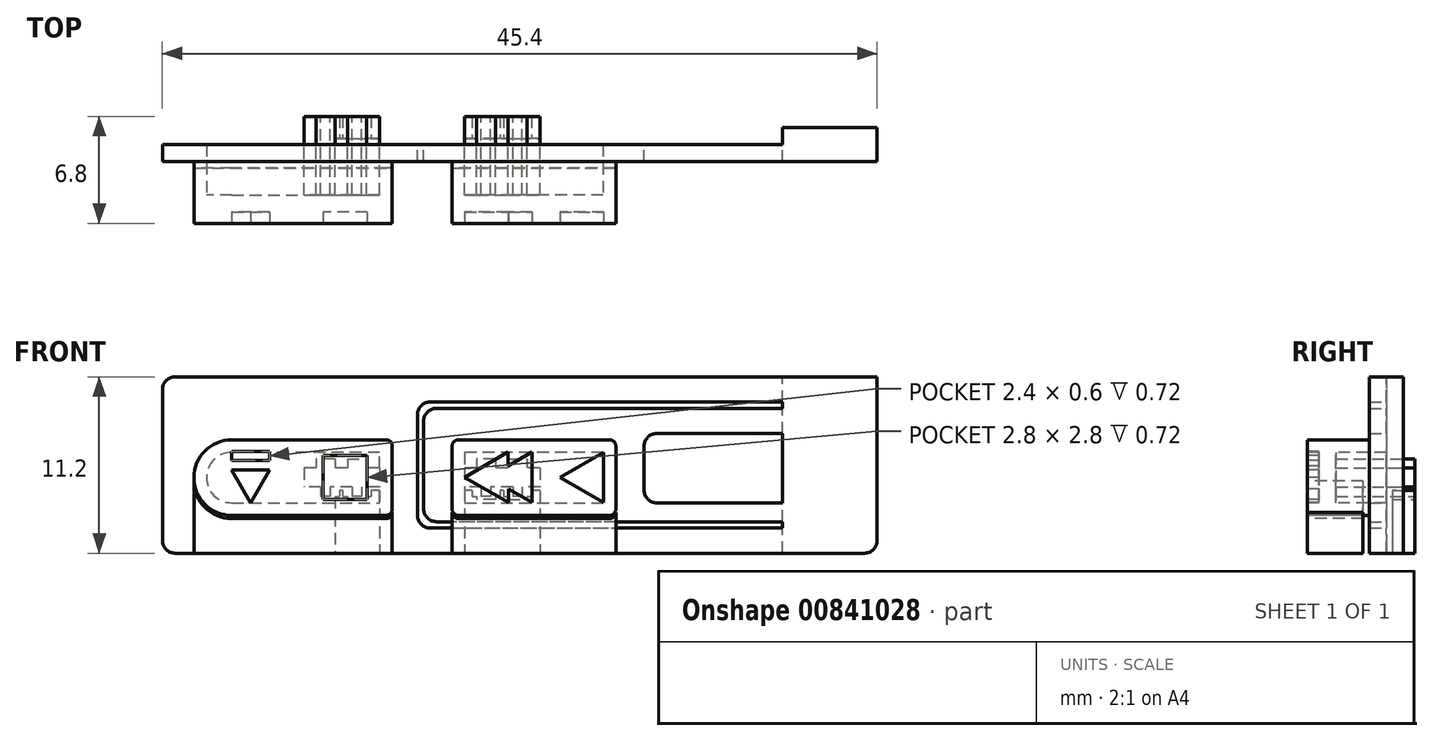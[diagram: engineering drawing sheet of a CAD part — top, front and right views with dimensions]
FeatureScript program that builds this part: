
annotation { "Feature Type Name" : "Feature", "Feature Type Description" : "" }
export const myFeature = defineFeature(function(context is Context, id is Id, definition is map)
    precondition{}
    {
        {
            var Q0;
            Q0=qCreatedBy(makeId("Front.planeOp"),FACE);
            var sketch = newSketch(context, id + "F0", { "sketchPlane" : qUnion([Q0])});
            skLineSegment(sketch, "E0.bottom", {"start": v(12.92, 2.7) * mm, "end": v(1.92, 2.7) * mm, "construction": true});
            skLineSegment(sketch, "E0.top", {"start": v(12.92, -2.7) * mm, "end": v(1.92, -2.7) * mm, "construction": true});
            skLineSegment(sketch, "E0.left", {"start": v(12.92, 2.7) * mm, "end": v(12.92, -2.7) * mm, "construction": true});
            skLineSegment(sketch, "E0.right", {"start": v(1.92, 2.7) * mm, "end": v(1.92, -2.7) * mm, "construction": true});
            skLineSegment(sketch, "E1.bottom", {"start": v(-1.28, 2.7) * mm, "end": v(-11.78, 2.7) * mm, "construction": true});
            skLineSegment(sketch, "E1.top", {"start": v(-1.28, -2.7) * mm, "end": v(-11.78, -2.7) * mm, "construction": true});
            skLineSegment(sketch, "E1.left", {"start": v(-1.28, 2.7) * mm, "end": v(-1.28, -2.7) * mm, "construction": true});
            skArc(sketch, "E2", {"start": v(-11.78, 2.7) * mm, "mid": v(-14.48, 0) * mm, "end": v(-11.78, -2.7) * mm, "construction": true});
            skLineSegment(sketch, "E3.0", {"start": v(-1.58, 2.4) * mm, "end": v(-11.78, 2.4) * mm});
            skLineSegment(sketch, "E3.1", {"start": v(-1.58, 2.4) * mm, "end": v(-1.58, -2.4) * mm});
            skLineSegment(sketch, "E3.2", {"start": v(-1.58, -2.4) * mm, "end": v(-11.78, -2.4) * mm});
            skArc(sketch, "E3.3", {"start": v(-11.78, 2.4) * mm, "mid": v(-14.18, 0) * mm, "end": v(-11.78, -2.4) * mm});
            skLineSegment(sketch, "E4.0", {"start": v(12.62, 2.4) * mm, "end": v(2.22, 2.4) * mm});
            skLineSegment(sketch, "E4.1", {"start": v(12.62, 2.4) * mm, "end": v(12.62, -2.4) * mm});
            skLineSegment(sketch, "E4.2", {"start": v(12.62, -2.4) * mm, "end": v(2.22, -2.4) * mm});
            skLineSegment(sketch, "E4.3", {"start": v(2.22, 2.4) * mm, "end": v(2.22, -2.4) * mm});
            skLineSegment(sketch, "E5.0", {"start": v(-2.38, 1.6) * mm, "end": v(-11.78, 1.6) * mm});
            skLineSegment(sketch, "E5.1", {"start": v(-2.38, 1.6) * mm, "end": v(-2.38, -1.6) * mm});
            skLineSegment(sketch, "E5.2", {"start": v(-2.38, -1.6) * mm, "end": v(-11.78, -1.6) * mm});
            skArc(sketch, "E5.3", {"start": v(-11.78, 1.6) * mm, "mid": v(-13.38, 0) * mm, "end": v(-11.78, -1.6) * mm});
            skLineSegment(sketch, "E6.0", {"start": v(3.02, 1.6) * mm, "end": v(3.02, -1.6) * mm});
            skLineSegment(sketch, "E6.1", {"start": v(11.82, 1.6) * mm, "end": v(3.02, 1.6) * mm});
            skLineSegment(sketch, "E6.2", {"start": v(11.82, 1.6) * mm, "end": v(11.82, -1.6) * mm});
            skLineSegment(sketch, "E6.3", {"start": v(11.82, -1.6) * mm, "end": v(3.02, -1.6) * mm});
            skLineSegment(sketch, "E7.0", {"start": v(0.02, 6.4) * mm, "end": v(0.02, -4.8) * mm});
            skLineSegment(sketch, "E8.0", {"start": v(0.42, 4.4) * mm, "end": v(0.42, -2.8) * mm});
            skLineSegment(sketch, "E9.0", {"start": v(29.22, 6.4) * mm, "end": v(-16.18, 6.4) * mm});
            skLineSegment(sketch, "E10.0", {"start": v(23.22, -4.8) * mm, "end": v(-16.18, -4.8) * mm});
            skLineSegment(sketch, "E11", {"start": v(-16.18, 6.4) * mm, "end": v(-16.18, -4.8) * mm});
            skLineSegment(sketch, "E12.0", {"start": v(23.22, 4.4) * mm, "end": v(0.42, 4.4) * mm});
            skLineSegment(sketch, "E13.MirrorCS", {"start": v(23.22, -2.8) * mm, "end": v(0.42, -2.8) * mm});
            skLineSegment(sketch, "E14.0", {"start": v(23.22, 4.8) * mm, "end": v(0.02, 4.8) * mm});
            skLineSegment(sketch, "E15", {"start": v(0.02, -3.2) * mm, "end": v(23.22, -3.2) * mm});
            skLineSegment(sketch, "E16", {"start": v(14.42, 4.4) * mm, "end": v(14.42, -2.8) * mm});
            skLineSegment(sketch, "E17", {"start": v(14.42, 2.8) * mm, "end": v(23.22, 2.8) * mm});
            skLineSegment(sketch, "E18", {"start": v(14.42, -1.6) * mm, "end": v(23.22, -1.6) * mm});
            skLineSegment(sketch, "E19", {"start": v(29.22, 6.4) * mm, "end": v(29.22, -4.8) * mm});
            skLineSegment(sketch, "E20", {"start": v(29.22, -4.8) * mm, "end": v(23.22, -4.8) * mm});
            skLineSegment(sketch, "E21", {"start": v(23.22, -4.8) * mm, "end": v(23.22, 6.4) * mm});
            skLineSegment(sketch, "E22.bottom", {"start": v(-2.38, 0.6) * mm, "end": v(-3.22, 0.6) * mm});
            skLineSegment(sketch, "E22.top", {"start": v(-2.38, -0.6) * mm, "end": v(-3.22, -0.6) * mm});
            skLineSegment(sketch, "E22.left", {"start": v(-2.38, 0.6) * mm, "end": v(-2.38, -0.6) * mm});
            skLineSegment(sketch, "E22.right", {"start": v(-7.18, 0.6) * mm, "end": v(-7.18, -0.6) * mm});
            skPoint(sketch, "E22.middle", {"position": v(-4.82, 0) * mm});
            skLineSegment(sketch, "E23.bottom", {"start": v(-5.22, 1.2) * mm, "end": v(-6.42, 1.2) * mm});
            skLineSegment(sketch, "E23.top", {"start": v(-5.22, -1.2) * mm, "end": v(-6.42, -1.2) * mm});
            skLineSegment(sketch, "E23.left", {"start": v(-5.22, 1.2) * mm, "end": v(-5.22, 0.6) * mm});
            skLineSegment(sketch, "E23.right", {"start": v(-6.42, 1.2) * mm, "end": v(-6.42, 0.6) * mm});
            skPoint(sketch, "E23.middle", {"position": v(-5.82, 0) * mm});
            skLineSegment(sketch, "E24", {"start": v(-4.82, 0.6) * mm, "end": v(-4.82, -0.6) * mm, "construction": true});
            skLineSegment(sketch, "E25.MirrorCS", {"start": v(-4.42, 1.2) * mm, "end": v(-4.42, 0.6) * mm});
            skLineSegment(sketch, "E26.MirrorCS", {"start": v(-3.22, 1.2) * mm, "end": v(-3.22, 0.6) * mm});
            skLineSegment(sketch, "E27.MirrorCS", {"start": v(-4.42, 1.2) * mm, "end": v(-3.22, 1.2) * mm});
            skLineSegment(sketch, "E28.MirrorCS", {"start": v(-4.42, -1.2) * mm, "end": v(-3.22, -1.2) * mm});
            skLineSegment(sketch, "E29.bottom", {"start": v(7.82, 0.6) * mm, "end": v(6.98, 0.6) * mm});
            skLineSegment(sketch, "E29.top", {"start": v(7.82, -0.6) * mm, "end": v(6.98, -0.6) * mm});
            skLineSegment(sketch, "E29.left", {"start": v(7.82, 0.6) * mm, "end": v(7.82, -0.6) * mm});
            skLineSegment(sketch, "E29.right", {"start": v(3.02, 0.6) * mm, "end": v(3.02, -0.6) * mm});
            skPoint(sketch, "E29.middle", {"position": v(5.38, 0) * mm});
            skLineSegment(sketch, "E30.bottom", {"start": v(4.98, 1.2) * mm, "end": v(3.78, 1.2) * mm});
            skLineSegment(sketch, "E30.top", {"start": v(4.98, -1.2) * mm, "end": v(3.78, -1.2) * mm});
            skLineSegment(sketch, "E30.left", {"start": v(4.98, 1.2) * mm, "end": v(4.98, 0.6) * mm});
            skLineSegment(sketch, "E30.right", {"start": v(3.78, 1.2) * mm, "end": v(3.78, 0.6) * mm});
            skPoint(sketch, "E30.middle", {"position": v(4.38, 0) * mm});
            skLineSegment(sketch, "E31", {"start": v(5.38, 0.6) * mm, "end": v(5.38, -0.6) * mm, "construction": true});
            skLineSegment(sketch, "E32.MirrorCS", {"start": v(5.78, 1.2) * mm, "end": v(5.78, 0.6) * mm});
            skLineSegment(sketch, "E33.MirrorCS", {"start": v(6.98, 1.2) * mm, "end": v(6.98, 0.6) * mm});
            skLineSegment(sketch, "E34.MirrorCS", {"start": v(5.78, 1.2) * mm, "end": v(6.98, 1.2) * mm});
            skLineSegment(sketch, "E35.MirrorCS", {"start": v(5.78, -1.2) * mm, "end": v(6.98, -1.2) * mm});
            skLineSegment(sketch, "E36", {"start": v(-6.42, 0.6) * mm, "end": v(-7.18, 0.6) * mm});
            skLineSegment(sketch, "E37", {"start": v(-6.42, -0.6) * mm, "end": v(-6.42, -1.2) * mm});
            skLineSegment(sketch, "E38", {"start": v(-6.42, -0.6) * mm, "end": v(-7.18, -0.6) * mm});
            skLineSegment(sketch, "E39", {"start": v(-5.22, -0.6) * mm, "end": v(-5.22, -1.2) * mm});
            skLineSegment(sketch, "E40", {"start": v(-4.42, -0.6) * mm, "end": v(-4.42, -1.2) * mm});
            skLineSegment(sketch, "E41", {"start": v(-4.42, -0.6) * mm, "end": v(-5.22, -0.6) * mm});
            skLineSegment(sketch, "E42", {"start": v(-4.42, 0.6) * mm, "end": v(-5.22, 0.6) * mm});
            skLineSegment(sketch, "E43.trimOffspring", {"start": v(-3.22, -0.6) * mm, "end": v(-3.22, -1.2) * mm});
            skLineSegment(sketch, "E44.trimOffspring", {"start": v(3.78, 0.6) * mm, "end": v(3.02, 0.6) * mm});
            skLineSegment(sketch, "E45.trimOffspring", {"start": v(3.78, -0.6) * mm, "end": v(3.78, -1.2) * mm});
            skLineSegment(sketch, "E46.trimOffspring", {"start": v(3.78, -0.6) * mm, "end": v(3.02, -0.6) * mm});
            skLineSegment(sketch, "E47.trimOffspring", {"start": v(4.98, -0.6) * mm, "end": v(4.98, -1.2) * mm});
            skLineSegment(sketch, "E48.trimOffspring", {"start": v(5.78, 0.6) * mm, "end": v(4.98, 0.6) * mm});
            skLineSegment(sketch, "E49.trimOffspring", {"start": v(6.98, -0.6) * mm, "end": v(6.98, -1.2) * mm});
            skLineSegment(sketch, "E50.trimOffspring", {"start": v(5.78, -0.6) * mm, "end": v(4.98, -0.6) * mm});
            skLineSegment(sketch, "E51.trimOffspring", {"start": v(5.78, -0.6) * mm, "end": v(5.78, -1.2) * mm});
            skSolve(sketch);
        }
        {
            var Q0;
            Q0=makeQuery(id+"F0.imprint","IMPRINT",FACE,{"disambiguationData":[TD([[makeQuery(id+"F0.imprint","IMPRINT",EDGE,{"derivedFrom":sQuery(id+"F0.wireOp",EDGE,"E22.bottom")}),1.0]])]});
            var Q1;
            Q1=makeQuery(id+"F0.imprint","IMPRINT",FACE,{"disambiguationData":[TD([[makeQuery(id+"F0.imprint","IMPRINT",EDGE,{"derivedFrom":sQuery(id+"F0.wireOp",EDGE,"E29.bottom")}),1.0]])]});
            extrude(context, id + "F1", {"entities" : qUnion([Q0, Q1]), "depth" : 6.8 * mm, "offsetDistance" : 25 * mm});
        }
        {
            var Q0;
            Q0=makeQuery(id+"F1.opExtrude","CAP_FACE",FACE,{"disambiguationData":[OSD([sQuery(id+"F0.wireOp",EDGE,"E22.bottom"),sQuery(id+"F0.wireOp",EDGE,"E22.top"),sQuery(id+"F0.wireOp",EDGE,"E22.left"),sQuery(id+"F0.wireOp",EDGE,"E22.right"),sQuery(id+"F0.wireOp",EDGE,"E23.bottom"),sQuery(id+"F0.wireOp",EDGE,"E23.top"),sQuery(id+"F0.wireOp",EDGE,"E23.left"),sQuery(id+"F0.wireOp",EDGE,"E23.right"),sQuery(id+"F0.wireOp",EDGE,"E25.MirrorCS"),sQuery(id+"F0.wireOp",EDGE,"E26.MirrorCS"),sQuery(id+"F0.wireOp",EDGE,"E27.MirrorCS"),sQuery(id+"F0.wireOp",EDGE,"E28.MirrorCS"),sQuery(id+"F0.wireOp",EDGE,"E36"),sQuery(id+"F0.wireOp",EDGE,"E37"),sQuery(id+"F0.wireOp",EDGE,"E38"),sQuery(id+"F0.wireOp",EDGE,"E39"),sQuery(id+"F0.wireOp",EDGE,"E40"),sQuery(id+"F0.wireOp",EDGE,"E41"),sQuery(id+"F0.wireOp",EDGE,"E42"),sQuery(id+"F0.wireOp",EDGE,"E43.trimOffspring")])],"isStart":false});
            var Q1;
            Q1=makeQuery(id+"F1.opExtrude","CAP_FACE",FACE,{"disambiguationData":[OSD([sQuery(id+"F0.wireOp",EDGE,"E29.bottom"),sQuery(id+"F0.wireOp",EDGE,"E29.top"),sQuery(id+"F0.wireOp",EDGE,"E29.left"),sQuery(id+"F0.wireOp",EDGE,"E29.right"),sQuery(id+"F0.wireOp",EDGE,"E30.bottom"),sQuery(id+"F0.wireOp",EDGE,"E30.top"),sQuery(id+"F0.wireOp",EDGE,"E30.left"),sQuery(id+"F0.wireOp",EDGE,"E30.right"),sQuery(id+"F0.wireOp",EDGE,"E32.MirrorCS"),sQuery(id+"F0.wireOp",EDGE,"E33.MirrorCS"),sQuery(id+"F0.wireOp",EDGE,"E34.MirrorCS"),sQuery(id+"F0.wireOp",EDGE,"E35.MirrorCS"),sQuery(id+"F0.wireOp",EDGE,"E44.trimOffspring"),sQuery(id+"F0.wireOp",EDGE,"E45.trimOffspring"),sQuery(id+"F0.wireOp",EDGE,"E46.trimOffspring"),sQuery(id+"F0.wireOp",EDGE,"E47.trimOffspring"),sQuery(id+"F0.wireOp",EDGE,"E48.trimOffspring"),sQuery(id+"F0.wireOp",EDGE,"E49.trimOffspring"),sQuery(id+"F0.wireOp",EDGE,"E50.trimOffspring"),sQuery(id+"F0.wireOp",EDGE,"E51.trimOffspring")])],"isStart":false});
            cPlane(context, id + "F2", {"entities" : qUnion([Q0, Q1]), "cplaneType" : CPlaneType.MID_PLANE, "offset" : 25 * mm, "width" : 150 * mm, "height" : 150 * mm});
        }
        {
            var Q0;
            Q0=qCreatedBy(id+"F2.planeOp",FACE);
            var sketch = newSketch(context, id + "F3", { "sketchPlane" : qUnion([Q0])});
            skLineSegment(sketch, "E52.0.0", {"start": v(-1.58, 2.4) * mm, "end": v(-11.78, 2.4) * mm});
            skArc(sketch, "E52.0.1", {"start": v(-11.78, 2.4) * mm, "mid": v(-14.18, 0) * mm, "end": v(-11.78, -2.4) * mm});
            skLineSegment(sketch, "E52.0.2", {"start": v(-11.78, -2.4) * mm, "end": v(-1.58, -2.4) * mm});
            skLineSegment(sketch, "E52.0.3", {"start": v(-1.58, -2.4) * mm, "end": v(-1.58, 2.4) * mm});
            skLineSegment(sketch, "E52.1.0", {"start": v(-6.42, -1.2) * mm, "end": v(-6.42, -0.6) * mm});
            skLineSegment(sketch, "E52.1.1", {"start": v(-6.42, -0.6) * mm, "end": v(-7.18, -0.6) * mm});
            skLineSegment(sketch, "E52.1.2", {"start": v(-7.18, -0.6) * mm, "end": v(-7.18, 0.6) * mm});
            skLineSegment(sketch, "E52.1.3", {"start": v(-7.18, 0.6) * mm, "end": v(-6.42, 0.6) * mm});
            skLineSegment(sketch, "E52.1.4", {"start": v(-6.42, 0.6) * mm, "end": v(-6.42, 1.2) * mm});
            skLineSegment(sketch, "E52.1.5", {"start": v(-6.42, 1.2) * mm, "end": v(-5.22, 1.2) * mm});
            skLineSegment(sketch, "E52.1.6", {"start": v(-5.22, 1.2) * mm, "end": v(-5.22, 0.6) * mm});
            skLineSegment(sketch, "E52.1.7", {"start": v(-5.22, 0.6) * mm, "end": v(-4.42, 0.6) * mm});
            skLineSegment(sketch, "E52.1.8", {"start": v(-4.42, 0.6) * mm, "end": v(-4.42, 1.2) * mm});
            skLineSegment(sketch, "E52.1.9", {"start": v(-4.42, 1.2) * mm, "end": v(-3.22, 1.2) * mm});
            skLineSegment(sketch, "E52.1.10", {"start": v(-3.22, 1.2) * mm, "end": v(-3.22, 0.6) * mm});
            skLineSegment(sketch, "E52.1.11", {"start": v(-3.22, 0.6) * mm, "end": v(-2.38, 0.6) * mm});
            skLineSegment(sketch, "E52.1.12", {"start": v(-2.38, 0.6) * mm, "end": v(-2.38, 1.6) * mm});
            skLineSegment(sketch, "E52.1.13", {"start": v(-2.38, 1.6) * mm, "end": v(-11.78, 1.6) * mm});
            skArc(sketch, "E52.1.14", {"start": v(-11.78, 1.6) * mm, "mid": v(-13.38, 0) * mm, "end": v(-11.78, -1.6) * mm});
            skLineSegment(sketch, "E52.1.15", {"start": v(-11.78, -1.6) * mm, "end": v(-2.38, -1.6) * mm});
            skLineSegment(sketch, "E52.1.16", {"start": v(-2.38, -1.6) * mm, "end": v(-2.38, -0.6) * mm});
            skLineSegment(sketch, "E52.1.17", {"start": v(-2.38, -0.6) * mm, "end": v(-3.22, -0.6) * mm});
            skLineSegment(sketch, "E52.1.18", {"start": v(-3.22, -0.6) * mm, "end": v(-3.22, -1.2) * mm});
            skLineSegment(sketch, "E52.1.19", {"start": v(-3.22, -1.2) * mm, "end": v(-4.42, -1.2) * mm});
            skLineSegment(sketch, "E52.1.20", {"start": v(-4.42, -1.2) * mm, "end": v(-4.42, -0.6) * mm});
            skLineSegment(sketch, "E52.1.21", {"start": v(-4.42, -0.6) * mm, "end": v(-5.22, -0.6) * mm});
            skLineSegment(sketch, "E52.1.22", {"start": v(-5.22, -0.6) * mm, "end": v(-5.22, -1.2) * mm});
            skLineSegment(sketch, "E52.1.23", {"start": v(-5.22, -1.2) * mm, "end": v(-6.42, -1.2) * mm});
            skLineSegment(sketch, "E52.2.0", {"start": v(3.78, -1.2) * mm, "end": v(3.78, -0.6) * mm});
            skLineSegment(sketch, "E52.2.1", {"start": v(3.78, -0.6) * mm, "end": v(3.02, -0.6) * mm});
            skLineSegment(sketch, "E52.2.2", {"start": v(3.02, -0.6) * mm, "end": v(3.02, -1.6) * mm});
            skLineSegment(sketch, "E52.2.3", {"start": v(3.02, -1.6) * mm, "end": v(11.82, -1.6) * mm});
            skLineSegment(sketch, "E52.2.4", {"start": v(11.82, -1.6) * mm, "end": v(11.82, 1.6) * mm});
            skLineSegment(sketch, "E52.2.5", {"start": v(11.82, 1.6) * mm, "end": v(3.02, 1.6) * mm});
            skLineSegment(sketch, "E52.2.6", {"start": v(3.02, 1.6) * mm, "end": v(3.02, 0.6) * mm});
            skLineSegment(sketch, "E52.2.7", {"start": v(3.02, 0.6) * mm, "end": v(3.78, 0.6) * mm});
            skLineSegment(sketch, "E52.2.8", {"start": v(3.78, 0.6) * mm, "end": v(3.78, 1.2) * mm});
            skLineSegment(sketch, "E52.2.9", {"start": v(3.78, 1.2) * mm, "end": v(4.98, 1.2) * mm});
            skLineSegment(sketch, "E52.2.10", {"start": v(4.98, 1.2) * mm, "end": v(4.98, 0.6) * mm});
            skLineSegment(sketch, "E52.2.11", {"start": v(4.98, 0.6) * mm, "end": v(5.78, 0.6) * mm});
            skLineSegment(sketch, "E52.2.12", {"start": v(5.78, 0.6) * mm, "end": v(5.78, 1.2) * mm});
            skLineSegment(sketch, "E52.2.13", {"start": v(5.78, 1.2) * mm, "end": v(6.98, 1.2) * mm});
            skLineSegment(sketch, "E52.2.14", {"start": v(6.98, 1.2) * mm, "end": v(6.98, 0.6) * mm});
            skLineSegment(sketch, "E52.2.15", {"start": v(6.98, 0.6) * mm, "end": v(7.82, 0.6) * mm});
            skLineSegment(sketch, "E52.2.16", {"start": v(7.82, 0.6) * mm, "end": v(7.82, -0.6) * mm});
            skLineSegment(sketch, "E52.2.17", {"start": v(7.82, -0.6) * mm, "end": v(6.98, -0.6) * mm});
            skLineSegment(sketch, "E52.2.18", {"start": v(6.98, -0.6) * mm, "end": v(6.98, -1.2) * mm});
            skLineSegment(sketch, "E52.2.19", {"start": v(6.98, -1.2) * mm, "end": v(5.78, -1.2) * mm});
            skLineSegment(sketch, "E52.2.20", {"start": v(5.78, -1.2) * mm, "end": v(5.78, -0.6) * mm});
            skLineSegment(sketch, "E52.2.21", {"start": v(5.78, -0.6) * mm, "end": v(4.98, -0.6) * mm});
            skLineSegment(sketch, "E52.2.22", {"start": v(4.98, -0.6) * mm, "end": v(4.98, -1.2) * mm});
            skLineSegment(sketch, "E52.2.23", {"start": v(4.98, -1.2) * mm, "end": v(3.78, -1.2) * mm});
            skLineSegment(sketch, "E52.3.0", {"start": v(12.62, 2.4) * mm, "end": v(2.22, 2.4) * mm});
            skLineSegment(sketch, "E52.3.1", {"start": v(2.22, 2.4) * mm, "end": v(2.22, -2.4) * mm});
            skLineSegment(sketch, "E52.3.2", {"start": v(2.22, -2.4) * mm, "end": v(12.62, -2.4) * mm});
            skLineSegment(sketch, "E52.3.3", {"start": v(12.62, -2.4) * mm, "end": v(12.62, 2.4) * mm});
            skLineSegment(sketch, "E53.0", {"start": v(-2.38, 1.6) * mm, "end": v(-2.38, -1.6) * mm});
            skPoint(sketch, "E53.1", {"position": v(3.02, 0) * mm});
            skSolve(sketch);
        }
        {
            var Q0;
            Q0=makeQuery(id+"F3.imprint","IMPRINT",FACE,{"disambiguationData":[TD([[makeQuery(id+"F3.imprint","IMPRINT",EDGE,{"derivedFrom":sQuery(id+"F3.wireOp",EDGE,"E52.1.0")}),1.0]])]});
            var Q1;
            Q1=makeQuery(id+"F3.imprint","IMPRINT",FACE,{"disambiguationData":[TD([[makeQuery(id+"F3.imprint","IMPRINT",EDGE,{"derivedFrom":sQuery(id+"F3.wireOp",EDGE,"E52.2.0")}),1.0]])]});
            extrude(context, id + "F4", {"entities" : qUnion([Q0, Q1]), "operationType" : NewBodyOperationType.ADD, "oppositeDirection" : true, "depth" : 1.8 * mm, "offsetDistance" : 25 * mm});
        }
        {
            var Q0;
            Q0=makeQuery(id+"F3.imprint","IMPRINT",FACE,{"disambiguationData":[TD([[makeQuery(id+"F3.imprint","IMPRINT",EDGE,{"derivedFrom":sQuery(id+"F3.wireOp",EDGE,"E52.0.0")}),1.0]])]});
            var Q1;
            Q1=makeQuery(id+"F3.imprint","IMPRINT",FACE,{"disambiguationData":[TD([[makeQuery(id+"F3.imprint","IMPRINT",EDGE,{"derivedFrom":sQuery(id+"F3.wireOp",EDGE,"E52.2.0")}),-1.0]])]});
            extrude(context, id + "F5", {"entities" : qUnion([Q0, Q1]), "operationType" : NewBodyOperationType.ADD, "oppositeDirection" : true, "depth" : 5 * mm, "offsetDistance" : 25 * mm});
        }
        {
            var Q0;
            Q0=qCreatedBy(makeId("Front.planeOp"),FACE);
            cPlane(context, id + "F6", {"entities" : qUnion([Q0]), "cplaneType" : CPlaneType.OFFSET, "offset" : 1.8 * mm, "width" : 150 * mm, "height" : 150 * mm});
        }
        {
            var Q0;
            Q0=qCreatedBy(id+"F6.planeOp",FACE);
            var sketch = newSketch(context, id + "F7", { "sketchPlane" : qUnion([Q0])});
            skLineSegment(sketch, "E54.0", {"start": v(-1.58, 2.4) * mm, "end": v(-11.78, 2.4) * mm});
            skArc(sketch, "E54.1", {"start": v(-11.78, 2.4) * mm, "mid": v(-14.18, 0) * mm, "end": v(-11.78, -2.4) * mm});
            skLineSegment(sketch, "E54.2", {"start": v(-1.58, -2.4) * mm, "end": v(-11.78, -2.4) * mm});
            skLineSegment(sketch, "E54.3", {"start": v(-1.58, 2.4) * mm, "end": v(-1.58, -2.4) * mm});
            skLineSegment(sketch, "E54.6", {"start": v(12.62, 2.4) * mm, "end": v(2.22, 2.4) * mm});
            skLineSegment(sketch, "E54.7", {"start": v(2.22, 2.4) * mm, "end": v(2.22, -2.4) * mm});
            skLineSegment(sketch, "E54.8", {"start": v(12.62, -2.4) * mm, "end": v(2.22, -2.4) * mm});
            skLineSegment(sketch, "E54.9", {"start": v(12.62, 2.4) * mm, "end": v(12.62, -2.4) * mm});
            skLineSegment(sketch, "E54.10", {"start": v(23.22, 4.4) * mm, "end": v(0.42, 4.4) * mm});
            skLineSegment(sketch, "E54.11", {"start": v(0.42, 4.4) * mm, "end": v(0.42, -2.8) * mm});
            skLineSegment(sketch, "E54.12", {"start": v(23.22, -2.8) * mm, "end": v(0.42, -2.8) * mm});
            skLineSegment(sketch, "E54.13", {"start": v(14.42, 4.4) * mm, "end": v(14.42, -2.8) * mm});
            skLineSegment(sketch, "E54.14", {"start": v(14.42, 2.8) * mm, "end": v(23.22, 2.8) * mm});
            skLineSegment(sketch, "E54.15", {"start": v(14.42, -1.6) * mm, "end": v(23.22, -1.6) * mm});
            skLineSegment(sketch, "E54.16", {"start": v(23.22, -4.8) * mm, "end": v(23.22, 6.4) * mm});
            skLineSegment(sketch, "E54.17", {"start": v(29.22, 6.4) * mm, "end": v(29.22, -4.8) * mm});
            skLineSegment(sketch, "E54.18", {"start": v(29.22, 6.4) * mm, "end": v(-16.18, 6.4) * mm});
            skLineSegment(sketch, "E54.19", {"start": v(29.22, -4.8) * mm, "end": v(23.22, -4.8) * mm});
            skLineSegment(sketch, "E54.20", {"start": v(23.22, 4.8) * mm, "end": v(0.02, 4.8) * mm});
            skLineSegment(sketch, "E54.21", {"start": v(0.02, 6.4) * mm, "end": v(0.02, -4.8) * mm});
            skLineSegment(sketch, "E54.22", {"start": v(23.22, -4.8) * mm, "end": v(-16.18, -4.8) * mm});
            skLineSegment(sketch, "E54.23", {"start": v(0.02, -3.2) * mm, "end": v(23.22, -3.2) * mm});
            skLineSegment(sketch, "E54.24", {"start": v(-16.18, 6.4) * mm, "end": v(-16.18, -4.8) * mm});
            skSolve(sketch);
        }
        {
            var Q0;
            {var subQ10=sQuery(id+"F7.wireOp",EDGE,"E54.17");Q0=makeQuery(id+"F7.imprint","IMPRINT",FACE,{"disambiguationData":[TD([[makeQuery(id+"F7.imprint","IMPRINT",EDGE,{"derivedFrom":subQ10}),-1.0]])]});}
            extrude(context, id + "F8", {"entities" : qUnion([Q0]), "endBound" : BoundingType.SYMMETRIC, "depth" : 2.16 * mm, "offsetDistance" : 25 * mm});
        }
        {
            var Q0;
            {var subQ3=sQuery(id+"F7.wireOp",EDGE,"E54.20");Q0=makeQuery(id+"F7.imprint","IMPRINT",FACE,{"disambiguationData":[TD([[makeQuery(id+"F7.imprint","IMPRINT",EDGE,{"derivedFrom":subQ3}),-1.0]])]});}
            var Q1;
            {var subQ5=sQuery(id+"F7.wireOp",EDGE,"E54.14");Q1=makeQuery(id+"F7.imprint","IMPRINT",FACE,{"disambiguationData":[TD([[makeQuery(id+"F7.imprint","IMPRINT",EDGE,{"derivedFrom":subQ5}),1.0]])]});}
            var Q2;
            {var subQ5=sQuery(id+"F7.wireOp",EDGE,"E54.15");Q2=makeQuery(id+"F7.imprint","IMPRINT",FACE,{"disambiguationData":[TD([[makeQuery(id+"F7.imprint","IMPRINT",EDGE,{"derivedFrom":subQ5}),-1.0]])]});}
            var Q3;
            {var subQ3=sQuery(id+"F7.wireOp",EDGE,"E54.23");Q3=makeQuery(id+"F7.imprint","IMPRINT",FACE,{"disambiguationData":[TD([[makeQuery(id+"F7.imprint","IMPRINT",EDGE,{"derivedFrom":subQ3}),-1.0]])]});}
            var Q4;
            Q4=makeQuery(id+"F7.imprint","IMPRINT",FACE,{"disambiguationData":[TD([[makeQuery(id+"F7.imprint","IMPRINT",EDGE,{"derivedFrom":sQuery(id+"F7.wireOp",EDGE,"E54.0")}),-1.0]])]});
            var Q5;
            Q5=makeQuery(id+"F7.imprint","IMPRINT",FACE,{"disambiguationData":[TD([[makeQuery(id+"F7.imprint","IMPRINT",EDGE,{"derivedFrom":sQuery(id+"F7.wireOp",EDGE,"E54.6")}),-1.0]])]});
            extrude(context, id + "F9", {"entities" : qUnion([Q0, Q1, Q2, Q3, Q4, Q5]), "operationType" : NewBodyOperationType.ADD, "depth" : 1.08 * mm, "offsetDistance" : 25 * mm});
        }
        {
            var Q0;
            Q0=makeQuery(id+"F9.opExtrude","SWEPT_EDGE",EDGE,{"disambiguationData":[OSD([sQuery(id+"F7.wireOp",EDGE,"E54.11"),sQuery(id+"F7.wireOp",EDGE,"E54.12")])]});
            var Q1;
            Q1=makeQuery(id+"F9.opExtrude","SWEPT_EDGE",EDGE,{"disambiguationData":[OSD([sQuery(id+"F7.wireOp",EDGE,"E54.10"),sQuery(id+"F7.wireOp",EDGE,"E54.11")])]});
            var Q2;
            Q2=makeQuery(id+"F9.opExtrude","SWEPT_EDGE",EDGE,{"disambiguationData":[OSD([sQuery(id+"F7.wireOp",EDGE,"E54.21"),sQuery(id+"F7.wireOp",EDGE,"E54.23")])]});
            var Q3;
            Q3=makeQuery(id+"F9.opExtrude","SWEPT_EDGE",EDGE,{"disambiguationData":[OSD([sQuery(id+"F7.wireOp",EDGE,"E54.20"),sQuery(id+"F7.wireOp",EDGE,"E54.21")])]});
            var Q4;
            Q4=makeQuery(id+"F9.opExtrude","SWEPT_EDGE",EDGE,{"disambiguationData":[OSD([sQuery(id+"F7.wireOp",EDGE,"E54.13"),sQuery(id+"F7.wireOp",EDGE,"E54.15")])]});
            var Q5;
            Q5=makeQuery(id+"F9.opExtrude","SWEPT_EDGE",EDGE,{"disambiguationData":[OSD([sQuery(id+"F7.wireOp",EDGE,"E54.13"),sQuery(id+"F7.wireOp",EDGE,"E54.14")])]});
            var Q6;
            Q6=makeQuery(id+"F9.opExtrude","SWEPT_EDGE",EDGE,{"disambiguationData":[OSD([sQuery(id+"F7.wireOp",EDGE,"E54.22"),sQuery(id+"F7.wireOp",EDGE,"E54.24")])]});
            var Q7;
            Q7=makeQuery(id+"F9.opExtrude","SWEPT_EDGE",EDGE,{"disambiguationData":[OSD([sQuery(id+"F7.wireOp",EDGE,"E54.18"),sQuery(id+"F7.wireOp",EDGE,"E54.24")])]});
            var Q8;
            Q8=makeQuery(id+"F8.opExtrude","SWEPT_EDGE",EDGE,{"disambiguationData":[OSD([sQuery(id+"F7.wireOp",EDGE,"E54.17"),sQuery(id+"F7.wireOp",EDGE,"E54.19")])]});
            fillet(context, id + "F10", {"entities" : qUnion([Q0, Q1, Q2, Q3, Q4, Q5, Q6, Q7, Q8]), "tangentPropagation" : true, "radius" : .8 * mm, "defaultsChanged" : false, "vertexSettings" : [], "allowEdgeOverflow" : false});
        }
        {
            var Q0;
            Q0=makeQuery(id+"F5.opExtrude","SWEPT_EDGE",EDGE,{"disambiguationData":[OSD([sQuery(id+"F3.wireOp",EDGE,"E52.0.2"),sQuery(id+"F3.wireOp",EDGE,"E52.0.3")])]});
            var Q1;
            Q1=makeQuery(id+"F5.opExtrude","SWEPT_EDGE",EDGE,{"disambiguationData":[OSD([sQuery(id+"F3.wireOp",EDGE,"E52.0.0"),sQuery(id+"F3.wireOp",EDGE,"E52.0.3")])]});
            var Q2;
            Q2=makeQuery(id+"F5.opExtrude","SWEPT_EDGE",EDGE,{"disambiguationData":[OSD([sQuery(id+"F3.wireOp",EDGE,"E52.3.0"),sQuery(id+"F3.wireOp",EDGE,"E52.3.1")])]});
            var Q3;
            Q3=makeQuery(id+"F5.opExtrude","SWEPT_EDGE",EDGE,{"disambiguationData":[OSD([sQuery(id+"F3.wireOp",EDGE,"E52.3.0"),sQuery(id+"F3.wireOp",EDGE,"E52.3.3")])]});
            var Q4;
            Q4=makeQuery(id+"F5.opExtrude","SWEPT_EDGE",EDGE,{"disambiguationData":[OSD([sQuery(id+"F3.wireOp",EDGE,"E52.3.2"),sQuery(id+"F3.wireOp",EDGE,"E52.3.3")])]});
            var Q5;
            Q5=makeQuery(id+"F5.opExtrude","SWEPT_EDGE",EDGE,{"disambiguationData":[OSD([sQuery(id+"F3.wireOp",EDGE,"E52.3.1"),sQuery(id+"F3.wireOp",EDGE,"E52.3.2")])]});
            fillet(context, id + "F11", {"entities" : qUnion([Q0, Q1, Q2, Q3, Q4, Q5]), "tangentPropagation" : true, "radius" : .4 * mm, "defaultsChanged" : false, "vertexSettings" : [], "allowEdgeOverflow" : false});
        }
        {
            var Q0;
            Q0=qCreatedBy(id+"F2.planeOp",FACE);
            var sketch = newSketch(context, id + "F12", { "sketchPlane" : qUnion([Q0])});
            skCircle(sketch, "E55.cCircle", {"center": v(10.92, 0) * mm, "radius": 1.85 * mm, "construction": true});
            skLineSegment(sketch, "E55.0", {"start": v(9.07, 0) * mm, "end": v(11.83, 1.61) * mm});
            skLineSegment(sketch, "E55.2", {"start": v(11.85, -1.59) * mm, "end": v(9.07, 0) * mm});
            skLineSegment(sketch, "E56.0", {"start": v(4.53, 0) * mm, "end": v(7.29, 1.62) * mm});
            skLineSegment(sketch, "E56.1", {"start": v(7.29, 1.62) * mm, "end": v(7.3, -1.58) * mm});
            skLineSegment(sketch, "E56.2", {"start": v(7.3, -1.58) * mm, "end": v(4.53, 0) * mm});
            skLineSegment(sketch, "E57.0", {"start": v(3.02, 0) * mm, "end": v(5.79, 1.62) * mm});
            skLineSegment(sketch, "E57.1", {"start": v(5.79, 1.62) * mm, "end": v(5.8, -1.58) * mm});
            skLineSegment(sketch, "E57.2", {"start": v(5.8, -1.58) * mm, "end": v(3.02, 0) * mm});
            skLineSegment(sketch, "E58", {"start": v(-10.58, -0.9) * mm, "end": v(-10.58, 0.48) * mm});
            skCircle(sketch, "E59.cCircle", {"center": v(-10.58, -0.21) * mm, "radius": 0.7 * mm, "construction": true});
            skLineSegment(sketch, "E59.0", {"start": v(-11.78, 0.48) * mm, "end": v(-9.38, 0.48) * mm});
            skLineSegment(sketch, "E59.1", {"start": v(-9.38, 0.48) * mm, "end": v(-10.58, -1.6) * mm});
            skLineSegment(sketch, "E59.2", {"start": v(-10.58, -1.6) * mm, "end": v(-11.78, 0.48) * mm});
            skPoint(sketch, "E59.0.midPoint", {"position": v(-10.58, 0.48) * mm});
            skLineSegment(sketch, "E60", {"start": v(-11.78, 1.08) * mm, "end": v(-11.78, 1.68) * mm});
            skLineSegment(sketch, "E61", {"start": v(-9.38, 1.08) * mm, "end": v(-9.38, 1.68) * mm});
            skLineSegment(sketch, "E62", {"start": v(-9.38, 1.08) * mm, "end": v(-11.78, 1.08) * mm});
            skLineSegment(sketch, "E63", {"start": v(-11.78, 1.68) * mm, "end": v(-9.38, 1.68) * mm});
            skLineSegment(sketch, "E64.bottom", {"start": v(-3.16, 1.4) * mm, "end": v(-5.96, 1.4) * mm});
            skLineSegment(sketch, "E64.top", {"start": v(-3.16, -1.4) * mm, "end": v(-5.96, -1.4) * mm});
            skLineSegment(sketch, "E64.left", {"start": v(-3.16, 1.4) * mm, "end": v(-3.16, -1.4) * mm});
            skLineSegment(sketch, "E64.right", {"start": v(-5.96, 1.4) * mm, "end": v(-5.96, -1.4) * mm});
            skLineSegment(sketch, "E65", {"start": v(11.85, -1.59) * mm, "end": v(11.83, 1.61) * mm});
            skLineSegment(sketch, "E66.MirrorCS", {"start": v(-7.16, 1.6) * mm, "end": v(-6.76, 1.6) * mm});
            skLineSegment(sketch, "E67.MirrorCS", {"start": v(-8.23, -1.6) * mm, "end": v(-7.83, -1.6) * mm});
            skLineSegment(sketch, "E68.MirrorCS", {"start": v(-7.83, -1.6) * mm, "end": v(-6.76, 1.6) * mm});
            skLineSegment(sketch, "E69.MirrorCS", {"start": v(-8.23, -1.6) * mm, "end": v(-7.16, 1.6) * mm});
            skSolve(sketch);
        }
        {
            var Q0;
            Q0=makeQuery(id+"F12.imprint","IMPRINT",FACE,{"disambiguationData":[TD([[makeQuery(id+"F12.imprint","IMPRINT",EDGE,{"derivedFrom":sQuery(id+"F12.wireOp",EDGE,"E55.0")}),-1.0]])]});
            var Q1;
            Q1=makeQuery(id+"F12.imprint","IMPRINT",FACE,{"disambiguationData":[TD([[makeQuery(id+"F12.imprint","IMPRINT",EDGE,{"derivedFrom":sQuery(id+"F12.wireOp",EDGE,"8GkAbv6F-Pd7l-cT7S-RkcG-G2hyiFPpfjUM")}),1.0]])]});
            var Q2;
            {var subQ0=sQuery(id+"F12.wireOp",EDGE,"E56.1");Q2=makeQuery(id+"F12.imprint","IMPRINT",FACE,{"disambiguationData":[TD([[makeQuery(id+"F12.imprint","IMPRINT",EDGE,{"derivedFrom":subQ0}),-1.0]])]});}
            var Q3;
            {var subQ0=sQuery(id+"F12.wireOp",EDGE,"E56.2");var subQ1=sQuery(id+"F12.wireOp",EDGE,"E56.0");var subQ2=makeQuery(id+"F12.imprint","INTERSECT",VERTEX,{"derivedFrom":[subQ1,subQ0]});Q3=makeQuery(id+"F12.imprint","IMPRINT",FACE,{"disambiguationData":[TD([[makeQuery(id+"F12.imprint","IMPRINT",EDGE,{"disambiguationData":[TD([[subQ2,-1.0]])],"derivedFrom":subQ1}),-1.0]])]});}
            var Q4;
            {var subQ1=sQuery(id+"F12.wireOp",EDGE,"E57.0");Q4=makeQuery(id+"F12.imprint","IMPRINT",FACE,{"disambiguationData":[TD([[makeQuery(id+"F12.imprint","IMPRINT",EDGE,{"derivedFrom":subQ1}),-1.0]])]});}
            var Q5;
            Q5=makeQuery(id+"F12.imprint","IMPRINT",FACE,{"disambiguationData":[TD([[makeQuery(id+"F12.imprint","IMPRINT",EDGE,{"derivedFrom":sQuery(id+"F12.wireOp",EDGE,"fa3466b0-8f12-48bf-adab-5b1b8b5b7c85.0")}),-1.0]])]});
            var Q6;
            Q6=makeQuery(id+"F12.imprint","IMPRINT",FACE,{"disambiguationData":[TD([[makeQuery(id+"F12.imprint","IMPRINT",EDGE,{"derivedFrom":sQuery(id+"F12.wireOp",EDGE,"79158872-b0d2-4b00-befb-ffface070bf3")}),1.0]])]});
            var Q7;
            {var subQ3=sQuery(id+"F12.wireOp",EDGE,"E59.1");Q7=makeQuery(id+"F12.imprint","IMPRINT",FACE,{"disambiguationData":[TD([[makeQuery(id+"F12.imprint","IMPRINT",EDGE,{"derivedFrom":subQ3}),-1.0]])]});}
            var Q8;
            Q8=makeQuery(id+"F12.imprint","IMPRINT",FACE,{"disambiguationData":[TD([[makeQuery(id+"F12.imprint","IMPRINT",EDGE,{"derivedFrom":sQuery(id+"F12.wireOp",EDGE,"E60")}),-1.0]])]});
            var Q9;
            Q9=makeQuery(id+"F12.imprint","IMPRINT",FACE,{"disambiguationData":[TD([[makeQuery(id+"F12.imprint","IMPRINT",EDGE,{"derivedFrom":sQuery(id+"F12.wireOp",EDGE,"E64.bottom")}),1.0]])]});
            extrude(context, id + "F13", {"entities" : qUnion([Q0, Q1, Q2, Q3, Q4, Q5, Q6, Q7, Q8, Q9]), "operationType" : NewBodyOperationType.REMOVE, "oppositeDirection" : true, "depth" : .72 * mm, "offsetDistance" : 25 * mm});
        }
        {
            var Q0;
            Q0=makeQuery(id+"F1.opExtrude","SWEPT_BODY",BODY,{"disambiguationData":[OSD([sQuery(id+"F0.wireOp",EDGE,"E22.bottom"),sQuery(id+"F0.wireOp",EDGE,"E22.top"),sQuery(id+"F0.wireOp",EDGE,"E22.left"),sQuery(id+"F0.wireOp",EDGE,"E22.right"),sQuery(id+"F0.wireOp",EDGE,"E23.bottom"),sQuery(id+"F0.wireOp",EDGE,"E23.top"),sQuery(id+"F0.wireOp",EDGE,"E23.left"),sQuery(id+"F0.wireOp",EDGE,"E23.right"),sQuery(id+"F0.wireOp",EDGE,"E25.MirrorCS"),sQuery(id+"F0.wireOp",EDGE,"E26.MirrorCS"),sQuery(id+"F0.wireOp",EDGE,"E27.MirrorCS"),sQuery(id+"F0.wireOp",EDGE,"E28.MirrorCS"),sQuery(id+"F0.wireOp",EDGE,"E36"),sQuery(id+"F0.wireOp",EDGE,"E37"),sQuery(id+"F0.wireOp",EDGE,"E38"),sQuery(id+"F0.wireOp",EDGE,"E39"),sQuery(id+"F0.wireOp",EDGE,"E40"),sQuery(id+"F0.wireOp",EDGE,"E41"),sQuery(id+"F0.wireOp",EDGE,"E42"),sQuery(id+"F0.wireOp",EDGE,"E43.trimOffspring")])]});
            var Q1;
            Q1=makeQuery(id+"F9.boolean.opBoolean","MERGE",EDGE,{"derivedFrom":[makeQuery(id+"F8.opExtrude","CAP_EDGE",EDGE,{"disambiguationData":[OSD([sQuery(id+"F7.wireOp",EDGE,"E54.19")])],"isStart":false}),makeQuery(id+"F9.opExtrude","CAP_EDGE",EDGE,{"disambiguationData":[OSD([sQuery(id+"F7.wireOp",EDGE,"E54.22")])],"isStart":false})]});
            var Q2;
            Q2=qCreatedBy(makeId("Origin.pointOp"),VERTEX);
            var Q3;
            Q3=qCreatedBy(makeId("Top.planeOp"),FACE);
            transform(context, id + "F14", {"entities" : qUnion([Q0]), "transformType" : TransformType.TRANSLATION_DISTANCE, "transformDirection" : qUnion([Q3]), "distance" : 4.8 * mm, "makeCopy" : false});
        }
        {
            var Q0;
            Q0=qCreatedBy(makeId("Top.planeOp"),FACE);
            var sketch = newSketch(context, id + "F15", { "sketchPlane" : qUnion([Q0])});
            skLineSegment(sketch, "E70.0.0", {"start": v(-11.78, -3.28) * mm, "end": v(-1.98, -3.28) * mm});
            skLineSegment(sketch, "E70.0.1", {"start": v(-1.98, -3.28) * mm, "end": v(-1.98, -6.8) * mm});
            skLineSegment(sketch, "E70.0.2", {"start": v(-1.98, -6.8) * mm, "end": v(-11.78, -6.8) * mm});
            skLineSegment(sketch, "E70.0.3", {"start": v(-11.78, -6.8) * mm, "end": v(-11.78, -3.28) * mm});
            skLineSegment(sketch, "E71", {"start": v(-14.18, -6.8) * mm, "end": v(-14.18, -3.28) * mm});
            skLineSegment(sketch, "E72.0.0", {"start": v(-1.58, -3.28) * mm, "end": v(-1.98, -3.28) * mm});
            skLineSegment(sketch, "E72.0.1", {"start": v(-1.58, -6.8) * mm, "end": v(-1.58, -3.28) * mm});
            skLineSegment(sketch, "E72.0.2", {"start": v(-1.58, -6.8) * mm, "end": v(-1.98, -6.8) * mm});
            skLineSegment(sketch, "E72.0.3", {"start": v(-1.98, -6.8) * mm, "end": v(-1.98, -3.28) * mm});
            skLineSegment(sketch, "E73.0.0", {"start": v(2.62, -3.28) * mm, "end": v(2.22, -3.28) * mm});
            skLineSegment(sketch, "E73.0.1", {"start": v(2.62, -6.8) * mm, "end": v(2.62, -3.28) * mm});
            skLineSegment(sketch, "E73.0.2", {"start": v(2.62, -6.8) * mm, "end": v(2.22, -6.8) * mm});
            skLineSegment(sketch, "E73.0.3", {"start": v(2.22, -6.8) * mm, "end": v(2.22, -3.28) * mm});
            skLineSegment(sketch, "E74.0.0", {"start": v(2.62, -3.28) * mm, "end": v(12.22, -3.28) * mm});
            skLineSegment(sketch, "E74.0.1", {"start": v(12.22, -3.28) * mm, "end": v(12.22, -6.8) * mm});
            skLineSegment(sketch, "E74.0.2", {"start": v(12.22, -6.8) * mm, "end": v(2.62, -6.8) * mm});
            skLineSegment(sketch, "E75.0.0", {"start": v(12.62, -3.28) * mm, "end": v(12.22, -3.28) * mm});
            skLineSegment(sketch, "E75.0.1", {"start": v(12.62, -6.8) * mm, "end": v(12.62, -3.28) * mm});
            skLineSegment(sketch, "E75.0.2", {"start": v(12.62, -6.8) * mm, "end": v(12.22, -6.8) * mm});
            skLineSegment(sketch, "E75.0.3", {"start": v(12.22, -6.8) * mm, "end": v(12.22, -3.28) * mm});
            skLineSegment(sketch, "E76.0.1", {"start": v(3.02, -1.4) * mm, "end": v(3.02, 0) * mm});
            skLineSegment(sketch, "E76.0.2", {"start": v(3.02, 0) * mm, "end": v(3.78, 0) * mm});
            skLineSegment(sketch, "E76.0.3", {"start": v(3.78, 0) * mm, "end": v(3.78, -1.4) * mm});
            skLineSegment(sketch, "E77.0.1", {"start": v(3.78, 0) * mm, "end": v(4.98, 0) * mm});
            skLineSegment(sketch, "E77.0.2", {"start": v(4.98, 0) * mm, "end": v(4.98, -1.4) * mm});
            skLineSegment(sketch, "E78.0.1", {"start": v(4.98, 0) * mm, "end": v(5.78, 0) * mm});
            skLineSegment(sketch, "E78.0.2", {"start": v(5.78, 0) * mm, "end": v(5.78, -1.4) * mm});
            skLineSegment(sketch, "E79.0.0", {"start": v(5.78, 0) * mm, "end": v(6.98, 0) * mm});
            skLineSegment(sketch, "E79.0.1", {"start": v(6.98, 0) * mm, "end": v(6.98, -1.4) * mm});
            skLineSegment(sketch, "E80.0.1", {"start": v(6.98, 0) * mm, "end": v(7.82, 0) * mm});
            skLineSegment(sketch, "E80.0.2", {"start": v(7.82, 0) * mm, "end": v(7.82, -1.4) * mm});
            skLineSegment(sketch, "E81.0.3", {"start": v(-3.22, 0) * mm, "end": v(-2.38, 0) * mm});
            skLineSegment(sketch, "E81.0.4", {"start": v(-2.38, 0) * mm, "end": v(-2.38, -1.4) * mm});
            skLineSegment(sketch, "E82.0.0", {"start": v(-3.22, 0) * mm, "end": v(-3.22, -1.4) * mm});
            skLineSegment(sketch, "E82.0.3", {"start": v(-4.42, 0) * mm, "end": v(-3.22, 0) * mm});
            skLineSegment(sketch, "E83.0.0", {"start": v(-4.42, 0) * mm, "end": v(-4.42, -1.4) * mm});
            skLineSegment(sketch, "E83.0.2", {"start": v(-5.22, -1.4) * mm, "end": v(-5.22, 0) * mm});
            skLineSegment(sketch, "E83.0.3", {"start": v(-5.22, 0) * mm, "end": v(-4.42, 0) * mm});
            skLineSegment(sketch, "E84.0.0", {"start": v(-5.22, 0) * mm, "end": v(-5.22, -1.4) * mm});
            skLineSegment(sketch, "E84.0.2", {"start": v(-6.42, -1.4) * mm, "end": v(-6.42, 0) * mm});
            skLineSegment(sketch, "E84.0.3", {"start": v(-6.42, 0) * mm, "end": v(-5.22, 0) * mm});
            skLineSegment(sketch, "E85.0.0", {"start": v(-6.42, 0) * mm, "end": v(-6.42, -1.4) * mm});
            skLineSegment(sketch, "E85.0.2", {"start": v(-7.18, -1.4) * mm, "end": v(-7.18, 0) * mm});
            skLineSegment(sketch, "E85.0.3", {"start": v(-7.18, 0) * mm, "end": v(-6.42, 0) * mm});
            skLineSegment(sketch, "E86.trimOffspring", {"start": v(-4.42, -1.4) * mm, "end": v(-4.42, 0) * mm});
            skLineSegment(sketch, "E87.trimOffspring", {"start": v(3.78, -1.4) * mm, "end": v(3.78, 0) * mm});
            skLineSegment(sketch, "E88.trimOffspring", {"start": v(6.98, -1.4) * mm, "end": v(6.98, 0) * mm});
            skLineSegment(sketch, "E89.trimOffspring", {"start": v(5.78, -1.4) * mm, "end": v(5.78, 0) * mm});
            skLineSegment(sketch, "E90.trimOffspring", {"start": v(4.98, -1.4) * mm, "end": v(4.98, 0) * mm});
            skLineSegment(sketch, "E91", {"start": v(-14.18, -6.8) * mm, "end": v(-11.78, -6.8) * mm});
            skLineSegment(sketch, "E92", {"start": v(-14.18, -3.28) * mm, "end": v(-11.78, -3.28) * mm});
            skLineSegment(sketch, "E93", {"start": v(-7.18, -1.4) * mm, "end": v(-2.38, -1.4) * mm});
            skLineSegment(sketch, "E94", {"start": v(3.02, -1.4) * mm, "end": v(7.82, -1.4) * mm});
            skSolve(sketch);
        }
        {
            var Q0;
            Q0=makeQuery(id+"F15.imprint","IMPRINT",FACE,{"disambiguationData":[TD([[makeQuery(id+"F15.imprint","IMPRINT",EDGE,{"derivedFrom":sQuery(id+"F15.wireOp",EDGE,"E70.0.0")}),-1.0]])]});
            var Q1;
            Q1=makeQuery(id+"F15.imprint","IMPRINT",FACE,{"disambiguationData":[TD([[makeQuery(id+"F15.imprint","IMPRINT",EDGE,{"derivedFrom":sQuery(id+"F15.wireOp",EDGE,"E70.0.3")}),1.0]])]});
            var Q2;
            Q2=makeQuery(id+"F15.imprint","IMPRINT",FACE,{"disambiguationData":[TD([[makeQuery(id+"F15.imprint","IMPRINT",EDGE,{"derivedFrom":sQuery(id+"F15.wireOp",EDGE,"E72.0.0")}),1.0]])]});
            var Q3;
            Q3=makeQuery(id+"F15.imprint","IMPRINT",FACE,{"disambiguationData":[TD([[makeQuery(id+"F15.imprint","IMPRINT",EDGE,{"derivedFrom":sQuery(id+"F15.wireOp",EDGE,"E73.0.0")}),1.0]])]});
            var Q4;
            Q4=makeQuery(id+"F15.imprint","IMPRINT",FACE,{"disambiguationData":[TD([[makeQuery(id+"F15.imprint","IMPRINT",EDGE,{"derivedFrom":sQuery(id+"F15.wireOp",EDGE,"E74.0.0")}),-1.0]])]});
            var Q5;
            Q5=makeQuery(id+"F15.imprint","IMPRINT",FACE,{"disambiguationData":[TD([[makeQuery(id+"F15.imprint","IMPRINT",EDGE,{"derivedFrom":sQuery(id+"F15.wireOp",EDGE,"E75.0.0")}),1.0]])]});
            var Q6;
            Q6=makeQuery(id+"F15.imprint","IMPRINT",FACE,{"disambiguationData":[TD([[makeQuery(id+"F15.imprint","IMPRINT",EDGE,{"derivedFrom":sQuery(id+"F15.wireOp",EDGE,"E80.0.1")}),-1.0]])]});
            var Q7;
            Q7=makeQuery(id+"F15.imprint","IMPRINT",FACE,{"disambiguationData":[TD([[makeQuery(id+"F15.imprint","IMPRINT",EDGE,{"derivedFrom":sQuery(id+"F15.wireOp",EDGE,"E79.0.0")}),-1.0]])]});
            var Q8;
            Q8=makeQuery(id+"F15.imprint","IMPRINT",FACE,{"disambiguationData":[TD([[makeQuery(id+"F15.imprint","IMPRINT",EDGE,{"derivedFrom":sQuery(id+"F15.wireOp",EDGE,"E78.0.1")}),-1.0]])]});
            var Q9;
            Q9=makeQuery(id+"F15.imprint","IMPRINT",FACE,{"disambiguationData":[TD([[makeQuery(id+"F15.imprint","IMPRINT",EDGE,{"derivedFrom":sQuery(id+"F15.wireOp",EDGE,"E77.0.1")}),-1.0]])]});
            var Q10;
            {var subQ0=sQuery(id+"F15.wireOp",EDGE,"E76.0.1");Q10=makeQuery(id+"F15.imprint","IMPRINT",FACE,{"disambiguationData":[TD([[makeQuery(id+"F15.imprint","IMPRINT",EDGE,{"derivedFrom":subQ0}),-1.0]])]});}
            var Q11;
            Q11=makeQuery(id+"F15.imprint","IMPRINT",FACE,{"disambiguationData":[TD([[makeQuery(id+"F15.imprint","IMPRINT",EDGE,{"derivedFrom":sQuery(id+"F15.wireOp",EDGE,"E81.0.3")}),-1.0]])]});
            var Q12;
            Q12=makeQuery(id+"F15.imprint","IMPRINT",FACE,{"disambiguationData":[TD([[makeQuery(id+"F15.imprint","IMPRINT",EDGE,{"derivedFrom":sQuery(id+"F15.wireOp",EDGE,"E82.0.3")}),-1.0]])]});
            var Q13;
            Q13=makeQuery(id+"F15.imprint","IMPRINT",FACE,{"disambiguationData":[TD([[makeQuery(id+"F15.imprint","IMPRINT",EDGE,{"derivedFrom":sQuery(id+"F15.wireOp",EDGE,"E83.0.3")}),-1.0]])]});
            var Q14;
            {var subQ0=sQuery(id+"F15.wireOp",EDGE,"E84.0.0");Q14=makeQuery(id+"F15.imprint","IMPRINT",FACE,{"disambiguationData":[TD([[makeQuery(id+"F15.imprint","IMPRINT",EDGE,{"derivedFrom":subQ0}),-1.0]])]});}
            var Q15;
            {var subQ0=sQuery(id+"F15.wireOp",EDGE,"E85.0.0");Q15=makeQuery(id+"F15.imprint","IMPRINT",FACE,{"disambiguationData":[TD([[makeQuery(id+"F15.imprint","IMPRINT",EDGE,{"derivedFrom":subQ0}),-1.0]])]});}
            extrude(context, id + "F16", {"entities" : qUnion([Q0, Q1, Q2, Q3, Q4, Q5, Q6, Q7, Q8, Q9, Q10, Q11, Q12, Q13, Q14, Q15]), "endBound" : BoundingType.UP_TO_NEXT, "depth" : 25 * mm, "hasOffset" : true, "offsetDistance" : .2 * mm});
        }
        {
            var Q0;
            Q0=makeQuery(id+"F1.opExtrude","SWEPT_FACE",FACE,{"disambiguationData":[OSD([sQuery(id+"F0.wireOp",EDGE,"E43.trimOffspring")])]});
            var Q1;
            Q1=makeQuery(id+"F1.opExtrude","SWEPT_FACE",FACE,{"disambiguationData":[OSD([sQuery(id+"F0.wireOp",EDGE,"E40")])]});
            var Q2;
            Q2=makeQuery(id+"F1.opExtrude","SWEPT_FACE",FACE,{"disambiguationData":[OSD([sQuery(id+"F0.wireOp",EDGE,"E39")])]});
            var Q3;
            Q3=makeQuery(id+"F1.opExtrude","SWEPT_FACE",FACE,{"disambiguationData":[OSD([sQuery(id+"F0.wireOp",EDGE,"E37")])]});
            extrude(context, id + "F17", {"entities" : qUnion([Q0, Q1, Q2, Q3]), "operationType" : NewBodyOperationType.REMOVE, "endBound" : BoundingType.SYMMETRIC, "oppositeDirection" : true, "depth" : .6 * mm, "offsetDistance" : 25 * mm});
        }
        {
            var Q0;
            Q0=makeQuery(id+"F1.opExtrude","SWEPT_FACE",FACE,{"disambiguationData":[OSD([sQuery(id+"F0.wireOp",EDGE,"E49.trimOffspring")])]});
            var Q1;
            Q1=makeQuery(id+"F1.opExtrude","SWEPT_FACE",FACE,{"disambiguationData":[OSD([sQuery(id+"F0.wireOp",EDGE,"E51.trimOffspring")])]});
            var Q2;
            Q2=makeQuery(id+"F1.opExtrude","SWEPT_FACE",FACE,{"disambiguationData":[OSD([sQuery(id+"F0.wireOp",EDGE,"E45.trimOffspring")])]});
            var Q3;
            Q3=makeQuery(id+"F1.opExtrude","SWEPT_FACE",FACE,{"disambiguationData":[OSD([sQuery(id+"F0.wireOp",EDGE,"E47.trimOffspring")])]});
            extrude(context, id + "F18", {"entities" : qUnion([Q0, Q1, Q2, Q3]), "operationType" : NewBodyOperationType.REMOVE, "endBound" : BoundingType.SYMMETRIC, "oppositeDirection" : true, "depth" : .6 * mm, "offsetDistance" : 25 * mm});
        }
    });
